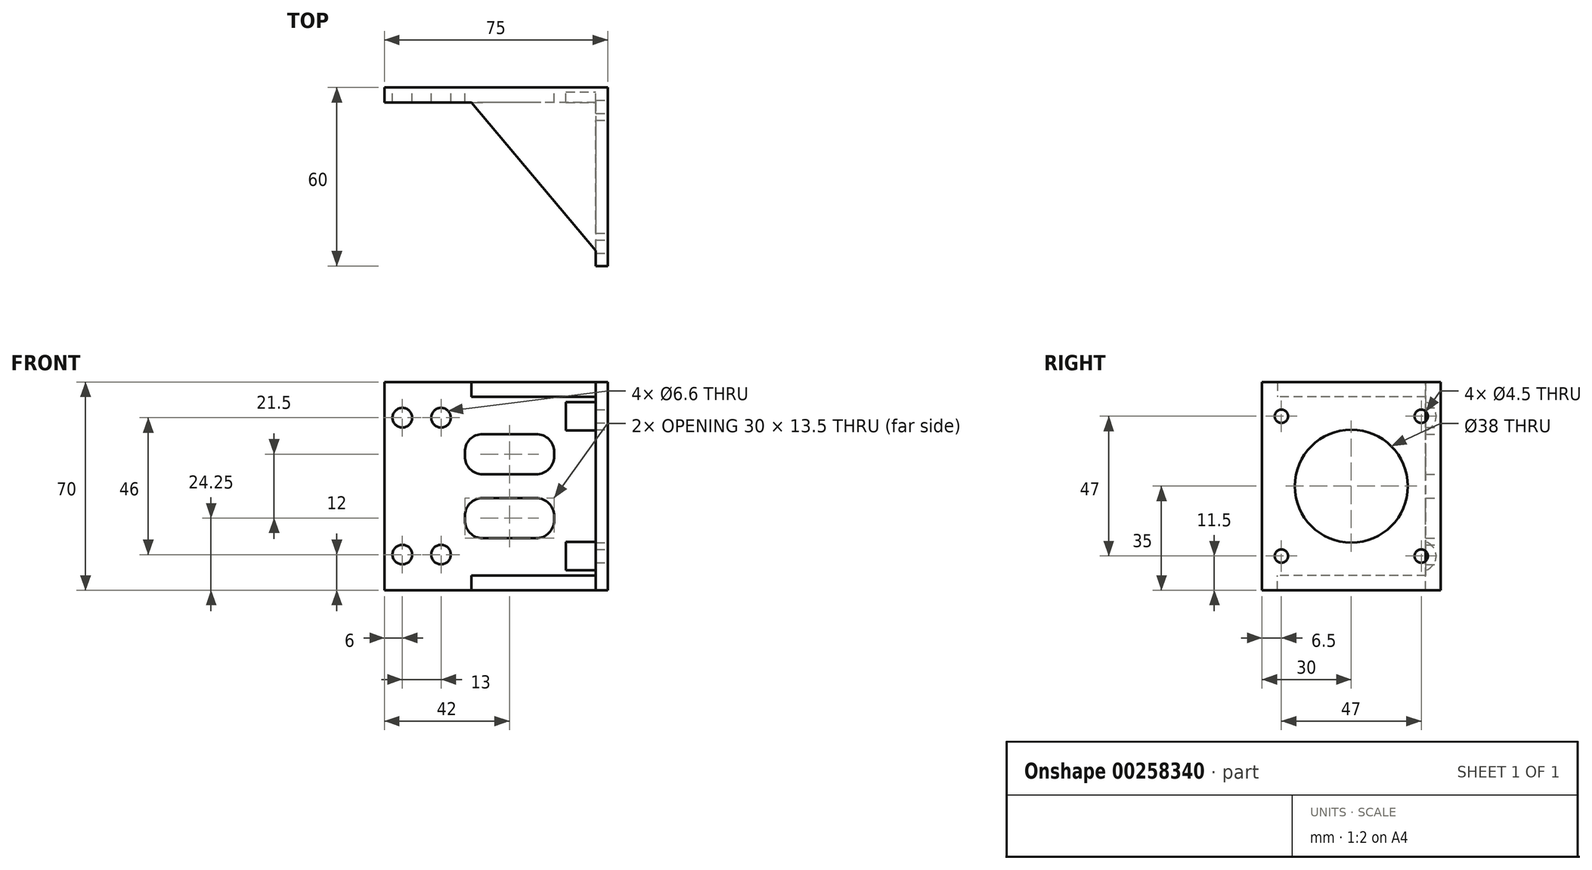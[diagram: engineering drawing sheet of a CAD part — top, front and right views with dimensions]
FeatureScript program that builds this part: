
annotation { "Feature Type Name" : "Feature", "Feature Type Description" : "" }
export const myFeature = defineFeature(function(context is Context, id is Id, definition is map)
    precondition{}
    {
        {
            var Q0;
            Q0=qCreatedBy(makeId("Front.planeOp"),FACE);
            var sketch = newSketch(context, id + "F0", { "sketchPlane" : qUnion([Q0])});
            skLineSegment(sketch, "E0.bottom", {"start": v(37.5, -35) * mm, "end": v(-37.5, -35) * mm});
            skLineSegment(sketch, "E0.top", {"start": v(37.5, 35) * mm, "end": v(-37.5, 35) * mm});
            skLineSegment(sketch, "E0.left", {"start": v(37.5, -35) * mm, "end": v(37.5, 35) * mm});
            skLineSegment(sketch, "E0.right", {"start": v(-37.5, -35) * mm, "end": v(-37.5, 35) * mm});
            skPoint(sketch, "E0.middle", {"position": v(0, 0) * mm});
            skLineSegment(sketch, "E1", {"start": v(-37.5, 0) * mm, "end": v(37.5, 0) * mm, "construction": true});
            skLineSegment(sketch, "E2.bottom", {"start": v(-37.5, 29.5) * mm, "end": v(-12.5, 29.5) * mm, "construction": true});
            skLineSegment(sketch, "E2.top", {"start": v(-37.5, -29.5) * mm, "end": v(-12.5, -29.5) * mm, "construction": true});
            skLineSegment(sketch, "E2.left", {"start": v(-37.5, 29.5) * mm, "end": v(-37.5, -29.5) * mm, "construction": true});
            skLineSegment(sketch, "E2.right", {"start": v(-12.5, 29.5) * mm, "end": v(-12.5, -29.5) * mm, "construction": true});
            skLineSegment(sketch, "E3", {"start": v(-25, 29.5) * mm, "end": v(-25, -29.5) * mm, "construction": true});
            skCircle(sketch, "E4", {"center": v(-31.5, 23) * mm, "radius": 3.3 * mm});
            skCircle(sketch, "E5.MirrorC", {"center": v(-18.5, 23) * mm, "radius": 3.3 * mm});
            skCircle(sketch, "E6.MirrorC", {"center": v(-18.5, -23) * mm, "radius": 3.3 * mm});
            skCircle(sketch, "E7.MirrorC", {"center": v(-31.5, -23) * mm, "radius": 3.3 * mm});
            skLineSegment(sketch, "E8.bottom", {"start": v(13.5, -10) * mm, "end": v(-4.5, -10) * mm, "construction": true});
            skLineSegment(sketch, "E8.top", {"start": v(13.5, 10) * mm, "end": v(-4.5, 10) * mm, "construction": true});
            skLineSegment(sketch, "E8.left", {"start": v(13.5, -10) * mm, "end": v(13.5, 10) * mm, "construction": true});
            skLineSegment(sketch, "E8.right", {"start": v(-4.5, -10) * mm, "end": v(-4.5, 10) * mm, "construction": true});
            skPoint(sketch, "E8.middle", {"position": v(4.5, 0) * mm});
            skLineSegment(sketch, "E9.bottom", {"start": v(19.5, -17.5) * mm, "end": v(-10.5, -17.5) * mm, "construction": true});
            skLineSegment(sketch, "E9.top", {"start": v(19.5, 17.5) * mm, "end": v(-10.5, 17.5) * mm, "construction": true});
            skLineSegment(sketch, "E9.left", {"start": v(19.5, -17.5) * mm, "end": v(19.5, 17.5) * mm, "construction": true});
            skLineSegment(sketch, "E9.right", {"start": v(-10.5, -17.5) * mm, "end": v(-10.5, 17.5) * mm, "construction": true});
            skLineSegment(sketch, "E10", {"start": v(19.5, 4) * mm, "end": v(-10.5, 4) * mm});
            skLineSegment(sketch, "E11", {"start": v(19.5, -4) * mm, "end": v(-10.5, -4) * mm});
            skLineSegment(sketch, "E12", {"start": v(-10.5, 4) * mm, "end": v(-10.5, 17.5) * mm});
            skLineSegment(sketch, "E13", {"start": v(19.5, 17.5) * mm, "end": v(19.5, 4) * mm});
            skLineSegment(sketch, "E14", {"start": v(19.5, -4) * mm, "end": v(19.5, -17.5) * mm});
            skLineSegment(sketch, "E15", {"start": v(-10.5, -17.5) * mm, "end": v(-10.5, -4) * mm});
            skLineSegment(sketch, "E16", {"start": v(-10.5, -17.5) * mm, "end": v(19.5, -17.5) * mm});
            skLineSegment(sketch, "E17", {"start": v(19.5, 17.5) * mm, "end": v(-10.5, 17.5) * mm});
            skSolve(sketch);
        }
        {
            var Q0;
            Q0=qSketchRegion(id+"F0",true);
            extrude(context, id + "F1", {"entities" : qUnion([Q0]), "depth" : 5 * mm});
        }
        {
            var Q0;
            Q0=makeQuery(id+"F1.opExtrude","CAP_FACE",FACE,{"disambiguationData":[OSD([sQuery(id+"F0.wireOp",EDGE,"E0.bottom"),sQuery(id+"F0.wireOp",EDGE,"E0.top"),sQuery(id+"F0.wireOp",EDGE,"E0.left"),sQuery(id+"F0.wireOp",EDGE,"E0.right"),sQuery(id+"F0.wireOp",EDGE,"E4"),sQuery(id+"F0.wireOp",EDGE,"E5.MirrorC"),sQuery(id+"F0.wireOp",EDGE,"E6.MirrorC"),sQuery(id+"F0.wireOp",EDGE,"E7.MirrorC")])],"isStart":false});
            var sketch = newSketch(context, id + "F2", { "sketchPlane" : qUnion([Q0])});
            skLineSegment(sketch, "E18.bottom", {"start": v(37.5, 35) * mm, "end": v(33.5, 35) * mm});
            skLineSegment(sketch, "E18.top", {"start": v(37.5, -35) * mm, "end": v(33.5, -35) * mm});
            skLineSegment(sketch, "E18.left", {"start": v(37.5, 35) * mm, "end": v(37.5, -35) * mm});
            skLineSegment(sketch, "E18.right", {"start": v(33.5, 35) * mm, "end": v(33.5, -35) * mm});
            skSolve(sketch);
        }
        {
            var Q0;
            Q0=qSketchRegion(id+"F2",true);
            extrude(context, id + "F3", {"entities" : qUnion([Q0]), "operationType" : NewBodyOperationType.ADD, "depth" : 55 * mm});
        }
        {
            var Q0;
            Q0=makeQuery(id+"F3.boolean.opBoolean","MERGE",FACE,{"derivedFrom":[makeQuery(id+"F1.opExtrude","SWEPT_FACE",FACE,{"disambiguationData":[OSD([sQuery(id+"F0.wireOp",EDGE,"E0.left")])]}),makeQuery(id+"F3.opExtrude","SWEPT_FACE",FACE,{"disambiguationData":[OSD([sQuery(id+"F2.wireOp",EDGE,"E18.left")])]})]});
            var sketch = newSketch(context, id + "F4", { "sketchPlane" : qUnion([Q0])});
            skLineSegment(sketch, "E19", {"start": v(-60, 0) * mm, "end": v(0, 0) * mm, "construction": true});
            skCircle(sketch, "E20", {"center": v(-30, 0) * mm, "radius": 19 * mm});
            skLineSegment(sketch, "E21.bottom", {"start": v(-6.5, -23.5) * mm, "end": v(-53.5, -23.5) * mm, "construction": true});
            skLineSegment(sketch, "E21.top", {"start": v(-6.5, 23.5) * mm, "end": v(-53.5, 23.5) * mm, "construction": true});
            skLineSegment(sketch, "E21.left", {"start": v(-6.5, -23.5) * mm, "end": v(-6.5, 23.5) * mm, "construction": true});
            skLineSegment(sketch, "E21.right", {"start": v(-53.5, -23.5) * mm, "end": v(-53.5, 23.5) * mm, "construction": true});
            skCircle(sketch, "E22", {"center": v(-53.5, 23.5) * mm, "radius": 2.25 * mm});
            skCircle(sketch, "E23", {"center": v(-6.5, 23.5) * mm, "radius": 2.25 * mm});
            skCircle(sketch, "E24", {"center": v(-6.5, -23.5) * mm, "radius": 2.25 * mm});
            skCircle(sketch, "E25", {"center": v(-53.5, -23.5) * mm, "radius": 2.25 * mm});
            skSolve(sketch);
        }
        {
            var Q0;
            Q0=qSketchRegion(id+"F4",true);
            var Q1;
            Q1=makeQuery(id+"F3.opExtrude","SWEPT_FACE",FACE,{"disambiguationData":[OSD([sQuery(id+"F2.wireOp",EDGE,"E18.right")])]});
            extrude(context, id + "F5", {"entities" : qUnion([Q0]), "operationType" : NewBodyOperationType.REMOVE, "endBound" : BoundingType.UP_TO_SURFACE, "oppositeDirection" : true, "endBoundEntityFace" : qUnion([Q1]), "depth" : 25 * mm});
        }
        {
            var Q0;
            Q0=sQuery(id+"F0.wireOp",EDGE,"E2.right");
            cPlane(context, id + "F6", {"entities" : qUnion([Q0]), "cplaneType" : CPlaneType.LINE_ANGLE, "offset" : 25 * mm, "angle" : 40 * degree, "oppositeDirection" : true, "width" : 150 * mm, "height" : 150 * mm});
        }
        {
            var Q0;
            Q0=qCreatedBy(id+"F6.planeOp",FACE);
            var sketch = newSketch(context, id + "F7", { "sketchPlane" : qUnion([Q0])});
            skLineSegment(sketch, "E26.0", {"start": v(24.1, 35) * mm, "end": v(-24.1, 35) * mm, "construction": true});
            skLineSegment(sketch, "E27.0", {"start": v(24.1, -35) * mm, "end": v(-24.1, -35) * mm, "construction": true});
            skLineSegment(sketch, "E28.bottom", {"start": v(-1.5, 35) * mm, "end": v(63.53, 35) * mm});
            skLineSegment(sketch, "E28.top", {"start": v(-1.5, 30) * mm, "end": v(63.53, 30) * mm});
            skLineSegment(sketch, "E28.left", {"start": v(-1.5, 35) * mm, "end": v(-1.5, 30) * mm});
            skLineSegment(sketch, "E28.right", {"start": v(63.53, 35) * mm, "end": v(63.53, 30) * mm});
            skLineSegment(sketch, "E29.MirrorCS", {"start": v(63.53, -35) * mm, "end": v(63.53, -30) * mm});
            skLineSegment(sketch, "E30.MirrorCS", {"start": v(-1.5, -35) * mm, "end": v(-1.5, -30) * mm});
            skLineSegment(sketch, "E31.MirrorCS", {"start": v(-1.5, -30) * mm, "end": v(63.53, -30) * mm});
            skLineSegment(sketch, "E32.MirrorCS", {"start": v(-1.5, -35) * mm, "end": v(63.53, -35) * mm});
            skSolve(sketch);
        }
        {
            var Q0;
            Q0=qSketchRegion(id+"F7",true);
            extrude(context, id + "F8", {"entities" : qUnion([Q0]), "operationType" : NewBodyOperationType.ADD, "endBound" : BoundingType.UP_TO_NEXT, "oppositeDirection" : true, "depth" : 25 * mm});
        }
        {
            var Q0;
            Q0=makeQuery(id+"F3.opExtrude","SWEPT_FACE",FACE,{"disambiguationData":[OSD([sQuery(id+"F2.wireOp",EDGE,"E18.right")])]});
            var sketch = newSketch(context, id + "F9", { "sketchPlane" : qUnion([Q0])});
            skCircle(sketch, "E33", {"center": v(6.5, 23.5) * mm, "radius": 5 * mm});
            skCircle(sketch, "E34", {"center": v(6.5, -23.5) * mm, "radius": 5 * mm});
            skSolve(sketch);
        }
        {
            var Q0;
            Q0 = qSketchRegion(id + "F9", true);
            extrude(context, id + "F10", {"entities" : qUnion([Q0]), "operationType" : NewBodyOperationType.REMOVE, "depth" : 10 * mm, "offsetDistance" : 25 * mm});
        }
        {
            var Q0;
            Q0=makeQuery(id+"F1.opExtrude","SWEPT_EDGE",EDGE,{"disambiguationData":[OSD([sQuery(id+"F0.wireOp",EDGE,"E12"),sQuery(id+"F0.wireOp",EDGE,"E17")])]});
            var Q1;
            Q1=makeQuery(id+"F1.opExtrude","SWEPT_EDGE",EDGE,{"disambiguationData":[OSD([sQuery(id+"F0.wireOp",EDGE,"E13"),sQuery(id+"F0.wireOp",EDGE,"E17")])]});
            var Q2;
            Q2=makeQuery(id+"F1.opExtrude","SWEPT_EDGE",EDGE,{"disambiguationData":[OSD([sQuery(id+"F0.wireOp",EDGE,"E10"),sQuery(id+"F0.wireOp",EDGE,"E13")])]});
            var Q3;
            Q3=makeQuery(id+"F1.opExtrude","SWEPT_EDGE",EDGE,{"disambiguationData":[OSD([sQuery(id+"F0.wireOp",EDGE,"E10"),sQuery(id+"F0.wireOp",EDGE,"E12")])]});
            var Q4;
            Q4=makeQuery(id+"F1.opExtrude","SWEPT_EDGE",EDGE,{"disambiguationData":[OSD([sQuery(id+"F0.wireOp",EDGE,"E11"),sQuery(id+"F0.wireOp",EDGE,"E14")])]});
            var Q5;
            Q5=makeQuery(id+"F1.opExtrude","SWEPT_EDGE",EDGE,{"disambiguationData":[OSD([sQuery(id+"F0.wireOp",EDGE,"E14"),sQuery(id+"F0.wireOp",EDGE,"E16")])]});
            var Q6;
            Q6=makeQuery(id+"F1.opExtrude","SWEPT_EDGE",EDGE,{"disambiguationData":[OSD([sQuery(id+"F0.wireOp",EDGE,"E15"),sQuery(id+"F0.wireOp",EDGE,"E16")])]});
            var Q7;
            Q7=makeQuery(id+"F1.opExtrude","SWEPT_EDGE",EDGE,{"disambiguationData":[OSD([sQuery(id+"F0.wireOp",EDGE,"E11"),sQuery(id+"F0.wireOp",EDGE,"E15")])]});
            fillet(context, id + "F11", {"entities" : qUnion([Q0, Q1, Q2, Q3, Q4, Q5, Q6, Q7]), "radius" : 6 * mm, "tangentPropagation" : true, "allowEdgeOverflow" : false});
        }
    });
